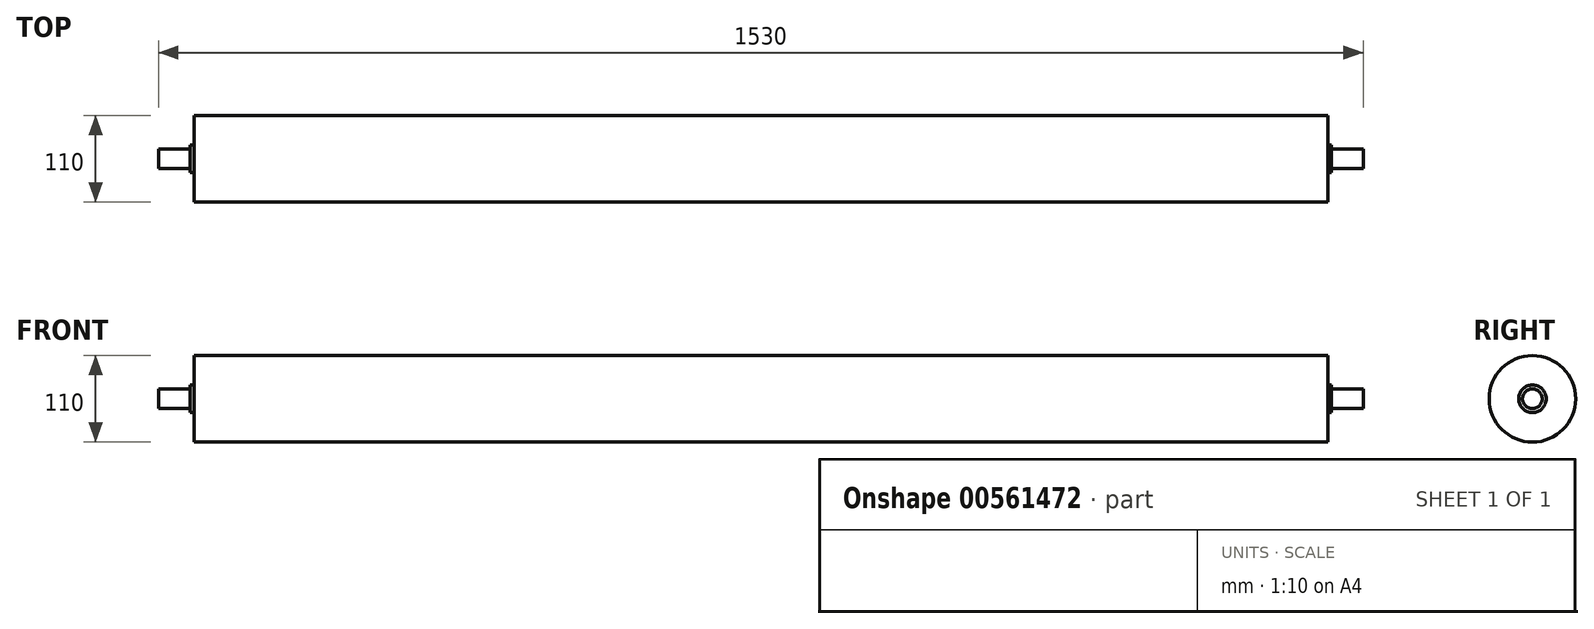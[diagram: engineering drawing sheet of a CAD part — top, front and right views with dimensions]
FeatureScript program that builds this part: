
annotation { "Feature Type Name" : "Feature", "Feature Type Description" : "" }
export const myFeature = defineFeature(function(context is Context, id is Id, definition is map)
    precondition{}
    {
        {
            var Q0;
            Q0=qCreatedBy(makeId("Front.planeOp"),FACE);
            var sketch = newSketch(context, id + "F0", { "sketchPlane" : qUnion([Q0])});
            skLineSegment(sketch, "E0", {"start": v(0, 0) * mm, "end": v(-765, 0) * mm});
            skLineSegment(sketch, "E1", {"start": v(-765, 0) * mm, "end": v(-765, 12.5) * mm});
            skLineSegment(sketch, "E2", {"start": v(-765, 12.5) * mm, "end": v(-725, 12.5) * mm});
            skLineSegment(sketch, "E3", {"start": v(-725, 12.5) * mm, "end": v(-725, 17.5) * mm});
            skLineSegment(sketch, "E4", {"start": v(-725, 17.5) * mm, "end": v(-720, 17.5) * mm});
            skLineSegment(sketch, "E5", {"start": v(-720, 17.5) * mm, "end": v(-720, 55) * mm});
            skLineSegment(sketch, "E6", {"start": v(-720, 55) * mm, "end": v(720, 55) * mm});
            skLineSegment(sketch, "E7", {"start": v(720, 55) * mm, "end": v(720, 17.5) * mm});
            skLineSegment(sketch, "E8", {"start": v(720, 17.5) * mm, "end": v(725, 17.5) * mm});
            skLineSegment(sketch, "E9", {"start": v(725, 17.5) * mm, "end": v(725, 12.5) * mm});
            skLineSegment(sketch, "E10", {"start": v(725, 12.5) * mm, "end": v(765, 12.5) * mm});
            skLineSegment(sketch, "E11", {"start": v(765, 12.5) * mm, "end": v(765, 0) * mm});
            skLineSegment(sketch, "E12", {"start": v(765, 0) * mm, "end": v(0, 0) * mm});
            skLineSegment(sketch, "E13", {"start": v(-776.42, 0) * mm, "end": v(773, 0) * mm, "construction": true});
            skSolve(sketch);
        }
        {
            var Q0;
            Q0=makeQuery(id+"F0.imprint","IMPRINT",FACE,{"disambiguationData":[TD([[makeQuery(id+"F0.imprint","IMPRINT",EDGE,{"derivedFrom":sQuery(id+"F0.wireOp",EDGE,"E0")}),-1.0]])]});
            var Q1;
            Q1=sQuery(id+"F0.wireOp",EDGE,"E13");
            revolve(context, id + "F1", {"entities" : qUnion([Q0]), "axis" : qUnion([Q1]), "revolveType" : RevolveType.FULL});
        }
    });
